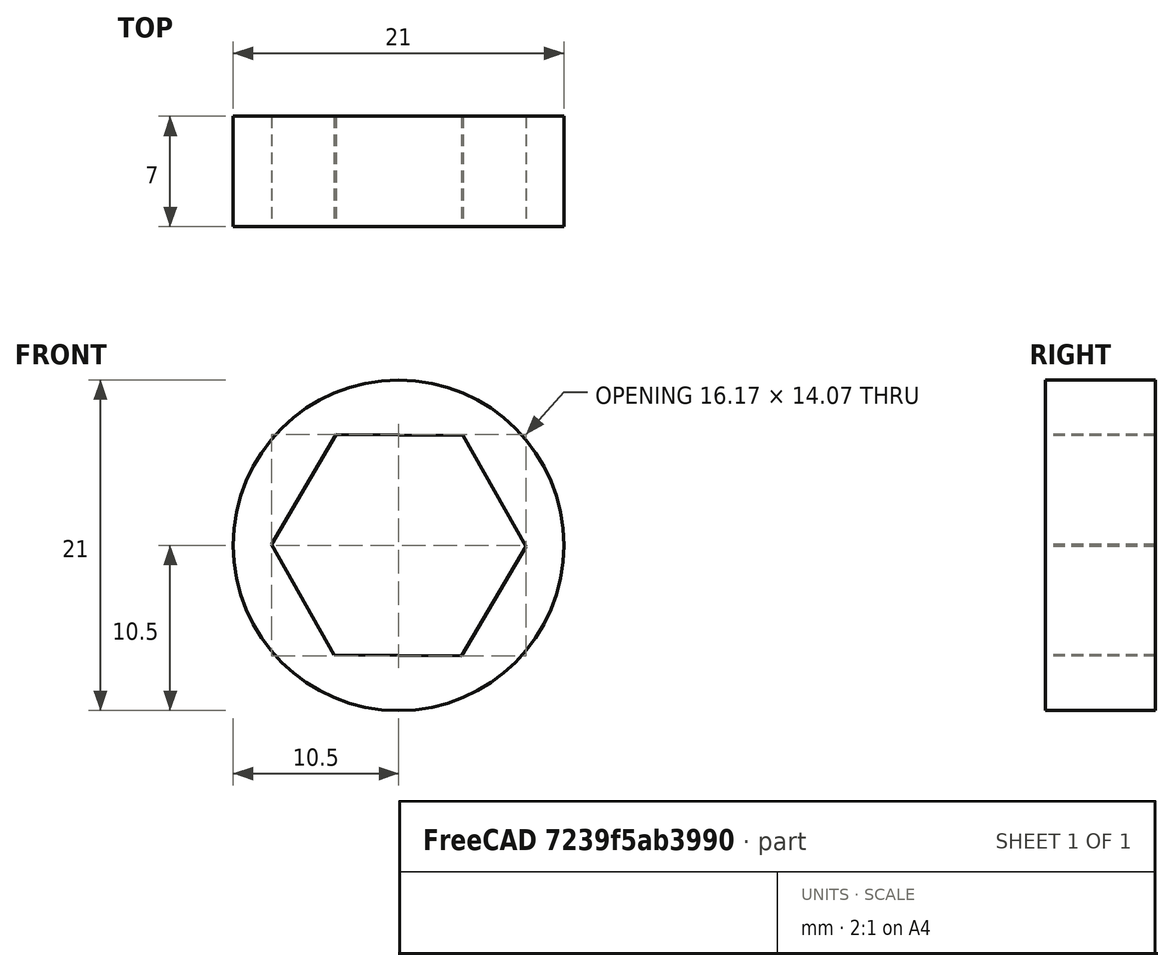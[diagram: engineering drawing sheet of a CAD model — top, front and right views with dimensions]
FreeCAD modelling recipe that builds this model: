
FCSTD DOCUMENT  (FreeCAD 0.21R33668 +26 (Git))
Label: arandela_eje
License: All rights reserved
LicenseURL: https://en.wikipedia.org/wiki/All_rights_reserved
objects: Sketcher::SketchObject×1, PartDesign::Pad×1, PartDesign::Body×1, App::Part×1
note: 4 computed .brp shape members not serialized (recipe doc carries the construction recipe); baked Part::Feature solids carry a one-line shape summary decoded from their .brp

FEATURE [Sketcher::SketchObject] Sketch
  FullyConstrained = false
  MapMode = 5
  Placement = pos=(0,0,0) rot=(1,0,0;1.5708rad)
  Support = -> [XZ_Plane001]
  sketch-geometry (8):
    g0: Circle CenterX=0 CenterY=0 CenterZ=0 NormalX=0 NormalY=0 NormalZ=1 AngleXU=0 Radius=10.5
    g1: LineSegment StartX=-3.98198 StartY=7.03433 StartZ=0 EndX=-8.0829 EndY=0.0686667 EndZ=0
    g2: LineSegment StartX=-8.0829 StartY=0.0686667 StartZ=0 EndX=-4.10092 EndY=-6.96567 EndZ=0
    g3: LineSegment StartX=-4.10092 StartY=-6.96567 StartZ=0 EndX=3.98198 EndY=-7.03433 EndZ=0
    g4: LineSegment StartX=3.98198 StartY=-7.03433 StartZ=0 EndX=8.0829 EndY=-0.0686667 EndZ=0
    g5: LineSegment StartX=8.0829 StartY=-0.0686667 StartZ=0 EndX=4.10092 EndY=6.96567 EndZ=0
    g6: LineSegment StartX=4.10092 StartY=6.96567 StartZ=0 EndX=-3.98198 EndY=7.03433 EndZ=0
    g7: Circle CenterX=0 CenterY=0 CenterZ=0 NormalX=0 NormalY=0 NormalZ=1 AngleXU=0 Radius=8.0832
  constraints (17):
    c: Coincident(g0,g-1)
    c: Diameter(g0) = 21
    c: Coincident(g1,g2)
    c: Coincident(g2,g3)
    c: Coincident(g3,g4)
    c: Coincident(g4,g5)
    c: Coincident(g5,g6)
    c: Coincident(g6,g1)
    c: Equal(g1, g2-g6) x5
    c: PointOnObject(g1,g7)
    c: PointOnObject(g2,g7)
    c: PointOnObject(g3,g7)
    c: PointOnObject(g4,g7)
    c: PointOnObject(g5,g7)
    c: PointOnObject(g6,g7)
    c: Coincident(g7,g0)
    c: DistanceY(g2,g1) = 14
FEATURE [PartDesign::Pad] Pad
  Direction = (0,-1,-2e-16)
  Length = 7
  Length2 = 10
  Placement = pos=(0,0,0) rot=(1,0,0;1.5708rad)
  Profile = -> Sketch
  ReferenceAxis = -> Sketch [N_Axis]
  Type = 0
FEATURE [PartDesign::Body] Body
  Group = -> [Sketch,Pad]
  Origin = -> Origin001
  Tip = -> Pad
FEATURE [App::Part] Part
  Group = -> [Body]
  Origin = -> Origin
